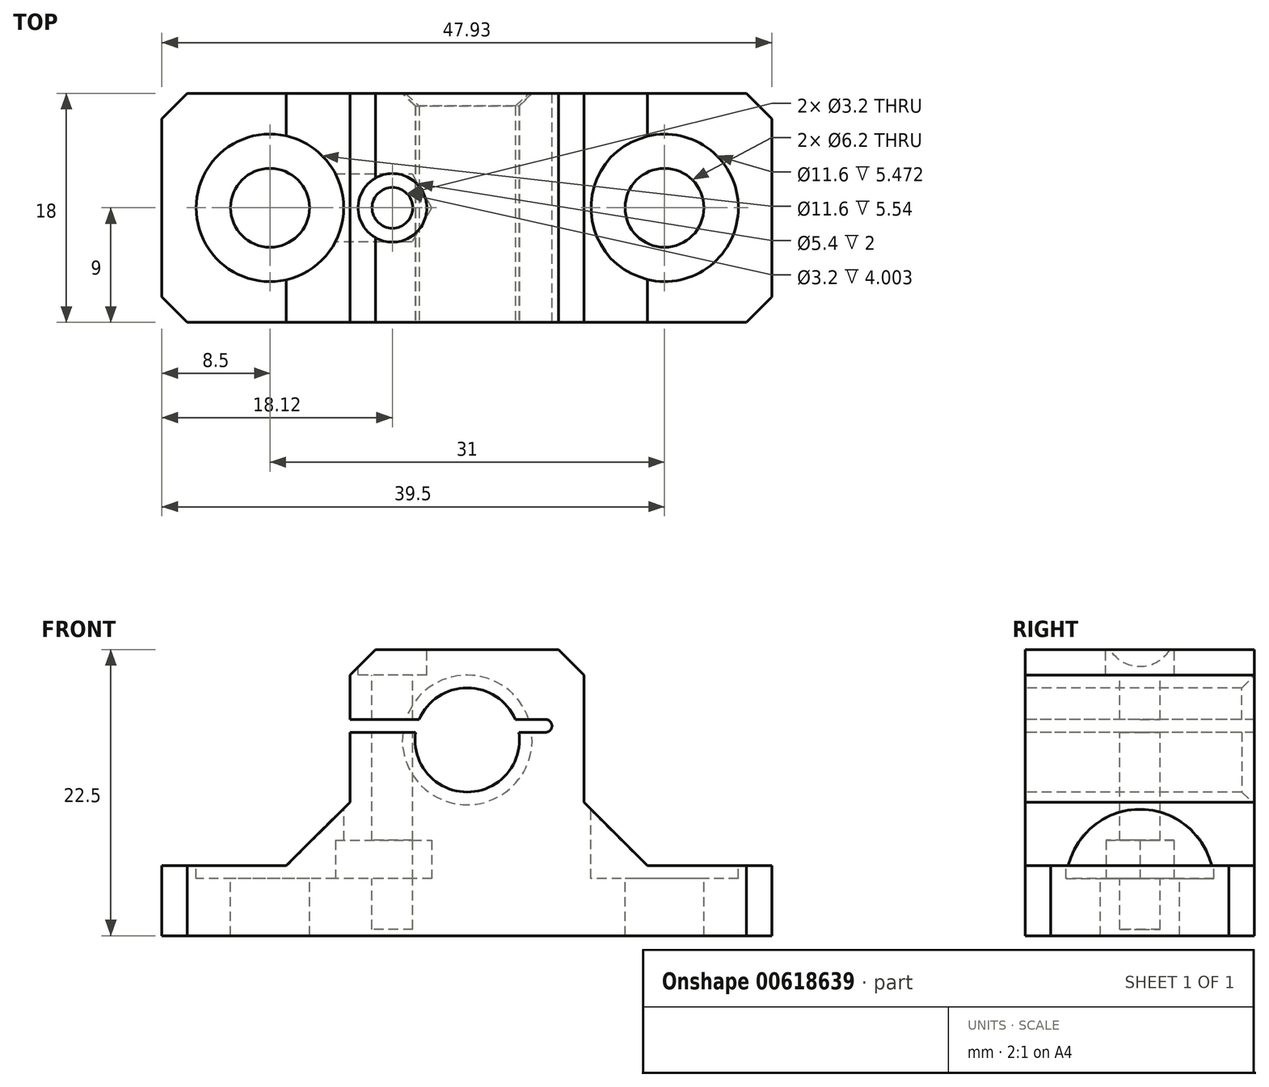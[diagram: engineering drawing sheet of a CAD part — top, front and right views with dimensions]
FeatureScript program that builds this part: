
annotation { "Feature Type Name" : "Feature", "Feature Type Description" : "" }
export const myFeature = defineFeature(function(context is Context, id is Id, definition is map)
    precondition{}
    {
        {
            var Q0;
            Q0=makeQuery(id+"FO52kGVbaD3jWPG.importOp","IMPORT",FACE,{"importTag":0.0});
            cPoint(context, id + "F0", {"pointType" : PointType.MESH_POINT, "mesh" : qUnion([Q0]), "x" : -6.2 * mm, "y" : -9.2 * mm, "z" : 8.5 * mm});
        }
        {
            var Q0;
            Q0=makeQuery(id+"FO52kGVbaD3jWPG.importOp","IMPORT",FACE,{"importTag":0.0});
            cPoint(context, id + "F1", {"pointType" : PointType.MESH_POINT, "mesh" : qUnion([Q0]), "x" : 6.2 * mm, "y" : -9.2 * mm, "z" : 8.5 * mm});
        }
        {
            var Q0;
            Q0=makeQuery(id+"FO52kGVbaD3jWPG.importOp","IMPORT",FACE,{"importTag":0.0});
            cPoint(context, id + "F2", {"pointType" : PointType.MESH_POINT, "mesh" : qUnion([Q0]), "x" : 24 * mm, "y" : -9.2 * mm, "z" : -8.5 * mm});
        }
        {
            var Q0;
            Q0=qCreatedBy(id+"F0",VERTEX);
            var Q1;
            Q1=qCreatedBy(id+"F1",VERTEX);
            var Q2;
            Q2=qCreatedBy(id+"F2",VERTEX);
            cPlane(context, id + "F3", {"entities" : qUnion([Q0, Q1, Q2]), "cplaneType" : CPlaneType.THREE_POINT, "offset" : 25 * mm, "width" : 150 * mm, "height" : 150 * mm});
        }
        {
            var Q0;
            Q0=qCreatedBy(id+"F3.planeOp",FACE);
            var sketch = newSketch(context, id + "F4", { "sketchPlane" : qUnion([Q0])});
            skPoint(sketch, "E0.0", {"position": v(-24, -8.5) * mm});
            skPoint(sketch, "E0.1", {"position": v(-24, -3) * mm});
            skPoint(sketch, "E0.2", {"position": v(-9.23, 8.5) * mm});
            skPoint(sketch, "E0.4", {"position": v(23.93, -3) * mm});
            skPoint(sketch, "E0.5", {"position": v(23.93, -8.5) * mm});
            skLineSegment(sketch, "E1", {"start": v(-24, -8.5) * mm, "end": v(-24, -3) * mm});
            skLineSegment(sketch, "E2", {"start": v(-9.23, 8.5) * mm, "end": v(-3.77, 8.5) * mm});
            skLineSegment(sketch, "E3", {"start": v(23.93, -3) * mm, "end": v(23.93, -8.5) * mm});
            skLineSegment(sketch, "E4", {"start": v(23.93, -8.5) * mm, "end": v(-24, -8.5) * mm});
            skPoint(sketch, "E5.0", {"position": v(3.77, 8.5) * mm});
            skLineSegment(sketch, "E6.bottom", {"start": v(-6.28, -8.5) * mm, "end": v(6.2, -8.5) * mm});
            skLineSegment(sketch, "E6.top", {"start": v(-6.28, -9.5) * mm, "end": v(6.2, -9.5) * mm});
            skLineSegment(sketch, "E6.left", {"start": v(-6.28, -8.5) * mm, "end": v(-6.28, -9.5) * mm});
            skLineSegment(sketch, "E6.right", {"start": v(6.2, -8.5) * mm, "end": v(6.2, -9.5) * mm});
            skLineSegment(sketch, "E7", {"start": v(9.16, 14) * mm, "end": v(9.16, -3) * mm});
            skLineSegment(sketch, "E8", {"start": v(9.16, -3) * mm, "end": v(23.93, -3) * mm});
            skLineSegment(sketch, "E9", {"start": v(-9.23, 7.5) * mm, "end": v(-9.23, -3) * mm});
            skLineSegment(sketch, "E10", {"start": v(-9.23, -3) * mm, "end": v(-24, -3) * mm});
            skPoint(sketch, "E11", {"position": v(0, 6.9) * mm});
            skArc(sketch, "E12", {"start": v(3.77, 8.5) * mm, "mid": v(0, 11) * mm, "end": v(-3.77, 8.5) * mm});
            skLineSegment(sketch, "E13.bottom", {"start": v(6.66, 8.5) * mm, "end": v(3.77, 8.5) * mm});
            skLineSegment(sketch, "E13.top", {"start": v(9.16, 14) * mm, "end": v(-9.23, 14) * mm});
            skLineSegment(sketch, "E13.right", {"start": v(-9.23, 8.5) * mm, "end": v(-9.23, 14) * mm});
            skLineSegment(sketch, "E14", {"start": v(6.66, 8.5) * mm, "end": v(6.66, 7.5) * mm});
            skLineSegment(sketch, "E15", {"start": v(6.66, 7.5) * mm, "end": v(4.05, 7.5) * mm});
            skLineSegment(sketch, "E16.trimOffspring", {"start": v(-3.77, 8.5) * mm, "end": v(-9.23, 8.5) * mm});
            skLineSegment(sketch, "E17.trimOffspring", {"start": v(-4.06, 7.5) * mm, "end": v(-9.23, 7.5) * mm});
            skLineSegment(sketch, "E18.trimOffspring", {"start": v(3.77, 8.5) * mm, "end": v(6.66, 8.5) * mm});
            skArc(sketch, "E19.trimOffspring", {"start": v(-4.06, 7.5) * mm, "mid": v(0, 2.8) * mm, "end": v(4.05, 7.5) * mm});
            skSolve(sketch);
        }
        {
            var Q0;
            Q0=makeQuery(id+"F4.imprint","IMPRINT",FACE,{"disambiguationData":[TD([[makeQuery(id+"F4.imprint","IMPRINT",EDGE,{"derivedFrom":sQuery(id+"F4.wireOp",EDGE,"E1")}),-1.0]])]});
            var Q1;
            Q1=makeQuery(id+"F4.imprint","IMPRINT",FACE,{"disambiguationData":[TD([[makeQuery(id+"F4.imprint","IMPRINT",EDGE,{"derivedFrom":sQuery(id+"F4.wireOp",EDGE,"E6.bottom")}),-1.0]])]});
            extrude(context, id + "F5", {"entities" : qUnion([Q0, Q1]), "oppositeDirection" : true, "depth" : 18 * mm, "offsetDistance" : 25 * mm});
        }
        {
            var Q0;
            Q0=makeQuery(id+"F5.opExtrude","SWEPT_FACE",FACE,{"disambiguationData":[OSD([sQuery(id+"F4.wireOp",EDGE,"E8")])]});
            var sketch = newSketch(context, id + "F6", { "sketchPlane" : qUnion([Q0])});
            skPoint(sketch, "E20.1", {"position": v(9.7, 8.8) * mm});
            skPoint(sketch, "E20.2", {"position": v(-9.7, 8.8) * mm});
            skPoint(sketch, "E20.3", {"position": v(-21.3, 8.8) * mm});
            skPoint(sketch, "E20.4", {"position": v(-21.3, -0.2) * mm});
            skPoint(sketch, "E20.5", {"position": v(-9.7, -0.2) * mm});
            skPoint(sketch, "E20.9", {"position": v(21.3, 8.8) * mm});
            skPoint(sketch, "E20.10", {"position": v(21.3, -0.2) * mm});
            skPoint(sketch, "E20.15", {"position": v(9.7, -0.2) * mm});
            skCircle(sketch, "E21", {"center": v(-15.5, -0.2) * mm, "radius": 3.1 * mm});
            skCircle(sketch, "E22", {"center": v(15.5, -0.2) * mm, "radius": 3.1 * mm});
            skCircle(sketch, "E23", {"center": v(15.5, -0.2) * mm, "radius": 5.8 * mm});
            skCircle(sketch, "E24", {"center": v(-15.5, -0.2) * mm, "radius": 5.8 * mm});
            skLineSegment(sketch, "E25", {"start": v(-21.3, -0.2) * mm, "end": v(-21.3, 8.8) * mm});
            skLineSegment(sketch, "E26", {"start": v(-21.3, 8.8) * mm, "end": v(-9.7, 8.8) * mm});
            skLineSegment(sketch, "E27", {"start": v(-9.7, 8.8) * mm, "end": v(-9.7, -0.2) * mm});
            skLineSegment(sketch, "E28", {"start": v(9.7, -0.2) * mm, "end": v(9.7, 8.8) * mm});
            skLineSegment(sketch, "E29", {"start": v(9.7, 8.8) * mm, "end": v(21.3, 8.8) * mm});
            skLineSegment(sketch, "E30", {"start": v(21.3, 8.8) * mm, "end": v(21.3, -0.2) * mm});
            skSolve(sketch);
        }
        {
            var Q0;
            Q0=makeQuery(id+"F6.imprint","IMPRINT",FACE,{"disambiguationData":[TD([[makeQuery(id+"F6.imprint","IMPRINT",EDGE,{"derivedFrom":sQuery(id+"F6.wireOp",EDGE,"E21")}),1.0]])]});
            var Q1;
            Q1=makeQuery(id+"F6.imprint","IMPRINT",FACE,{"disambiguationData":[TD([[makeQuery(id+"F6.imprint","IMPRINT",EDGE,{"derivedFrom":sQuery(id+"F6.wireOp",EDGE,"E22")}),1.0]])]});
            extrude(context, id + "F7", {"entities" : qUnion([Q0, Q1]), "operationType" : NewBodyOperationType.REMOVE, "oppositeDirection" : true, "depth" : 6 * mm, "offsetDistance" : 25 * mm});
        }
        {
            var Q0;
            Q0=makeQuery(id+"F6.imprint","IMPRINT",FACE,{"disambiguationData":[TD([[makeQuery(id+"F6.imprint","IMPRINT",EDGE,{"derivedFrom":sQuery(id+"F6.wireOp",EDGE,"E21")}),-1.0]])]});
            var Q1;
            Q1=makeQuery(id+"F6.imprint","IMPRINT",FACE,{"disambiguationData":[TD([[makeQuery(id+"F6.imprint","IMPRINT",EDGE,{"derivedFrom":sQuery(id+"F6.wireOp",EDGE,"E22")}),-1.0]])]});
            extrude(context, id + "F8", {"entities" : qUnion([Q0, Q1]), "operationType" : NewBodyOperationType.REMOVE, "oppositeDirection" : true, "depth" : 1 * mm, "offsetDistance" : 25 * mm});
        }
        {
            var Q0;
            Q0=makeQuery(id+"F5.opExtrude","SWEPT_FACE",FACE,{"disambiguationData":[OSD([sQuery(id+"F4.wireOp",EDGE,"E3")])]});
            cPlane(context, id + "F9", {"entities" : qUnion([Q0]), "cplaneType" : CPlaneType.OFFSET, "offset" : 0 * mm, "oppositeDirection" : true, "width" : 150 * mm, "height" : 150 * mm});
        }
        {
            var Q0;
            Q0=qCreatedBy(id+"F9.planeOp",FACE);
            var sketch = newSketch(context, id + "F10", { "sketchPlane" : qUnion([Q0])});
            skLineSegment(sketch, "E31", {"start": v(3.9, -10.2) * mm, "end": v(3.9, -8.89) * mm});
            skLineSegment(sketch, "E32.top", {"start": v(3.9, -8.89) * mm, "end": v(4.4, -8.89) * mm});
            skLineSegment(sketch, "E32.right", {"start": v(4.4, -8.5) * mm, "end": v(4.4, -8.89) * mm});
            skLineSegment(sketch, "E33.0", {"start": v(4.4, -8.5) * mm, "end": v(-4.8, -8.5) * mm});
            skLineSegment(sketch, "E34", {"start": v(-4.3, -10.2) * mm, "end": v(3.9, -10.2) * mm});
            skLineSegment(sketch, "E35.0", {"start": v(8.8, -8.5) * mm, "end": v(-9.2, -8.5) * mm});
            skLineSegment(sketch, "E35.1", {"start": v(-9.2, -8.5) * mm, "end": v(-9.2, -9.5) * mm});
            skLineSegment(sketch, "E35.2", {"start": v(8.8, -9.5) * mm, "end": v(-9.2, -9.5) * mm});
            skLineSegment(sketch, "E35.3", {"start": v(8.8, -8.5) * mm, "end": v(8.8, -9.5) * mm});
            skLineSegment(sketch, "E36", {"start": v(-4.8, -8.5) * mm, "end": v(-3.1, -10.2) * mm});
            skSolve(sketch);
        }
        {
            var Q0;
            {var subQ3=sQuery(id+"F10.wireOp",EDGE,"E31");Q0=makeQuery(id+"F10.imprint","IMPRINT",FACE,{"disambiguationData":[TD([[makeQuery(id+"F10.imprint","IMPRINT",EDGE,{"derivedFrom":subQ3}),-1.0]])]});}
            var Q1;
            {var subQ0=sQuery(id+"F10.wireOp",EDGE,"E35.1");Q1=makeQuery(id+"F10.imprint","IMPRINT",FACE,{"disambiguationData":[TD([[makeQuery(id+"F10.imprint","IMPRINT",EDGE,{"derivedFrom":subQ0}),1.0]])]});}
            extrude(context, id + "F11", {"entities" : qUnion([Q0, Q1]), "operationType" : NewBodyOperationType.REMOVE, "oppositeDirection" : true, "depth" : 31 * mm, "offsetDistance" : 25 * mm});
        }
        {
            var Q0;
            Q0=makeQuery(id+"F5.opExtrude","SWEPT_EDGE",EDGE,{"disambiguationData":[OSD([sQuery(id+"F4.wireOp",EDGE,"E9"),sQuery(id+"F4.wireOp",EDGE,"E10")])]});
            var Q1;
            Q1=makeQuery(id+"F5.opExtrude","SWEPT_EDGE",EDGE,{"disambiguationData":[OSD([sQuery(id+"F4.wireOp",EDGE,"E7"),sQuery(id+"F4.wireOp",EDGE,"E8")])]});
            chamfer(context, id + "F12", {"entities" : qUnion([Q0, Q1]), "width" : 5 * mm, "tangentPropagation" : true});
        }
        {
            var Q0;
            Q0=makeQuery(id+"F5.opExtrude","SWEPT_EDGE",EDGE,{"disambiguationData":[OSD([sQuery(id+"F4.wireOp",EDGE,"E13.top"),sQuery(id+"F4.wireOp",EDGE,"E13.left")])]});
            var Q1;
            Q1=makeQuery(id+"F5.opExtrude","SWEPT_EDGE",EDGE,{"disambiguationData":[OSD([sQuery(id+"F4.wireOp",EDGE,"E13.top"),sQuery(id+"F4.wireOp",EDGE,"E13.right")])]});
            var Q2;
            Q2=makeQuery(id+"F5.opExtrude","CAP_EDGE",EDGE,{"disambiguationData":[OSD([sQuery(id+"F4.wireOp",EDGE,"E1")])],"isStart":true});
            var Q3;
            Q3=makeQuery(id+"F5.opExtrude","CAP_EDGE",EDGE,{"disambiguationData":[OSD([sQuery(id+"F4.wireOp",EDGE,"E1")])],"isStart":false});
            var Q4;
            Q4=makeQuery(id+"F5.opExtrude","CAP_EDGE",EDGE,{"disambiguationData":[OSD([sQuery(id+"F4.wireOp",EDGE,"E3")])],"isStart":true});
            var Q5;
            Q5=makeQuery(id+"F5.opExtrude","CAP_EDGE",EDGE,{"disambiguationData":[OSD([sQuery(id+"F4.wireOp",EDGE,"E3")])],"isStart":false});
            chamfer(context, id + "F13", {"entities" : qUnion([Q0, Q1, Q2, Q3, Q4, Q5]), "width" : 2 * mm, "tangentPropagation" : true});
        }
        {
            var Q0;
            Q0=makeQuery(id+"F5.opExtrude","CAP_EDGE",EDGE,{"disambiguationData":[OSD([sQuery(id+"F4.wireOp",EDGE,"E19.trimOffspring")])],"isStart":false});
            var Q1;
            Q1=makeQuery(id+"F5.opExtrude","CAP_EDGE",EDGE,{"disambiguationData":[OSD([sQuery(id+"F4.wireOp",EDGE,"E12")])],"isStart":false});
            chamfer(context, id + "F14", {"entities" : qUnion([Q0, Q1]), "width" : 1 * mm, "tangentPropagation" : true});
        }
        {
            var Q0;
            Q0=makeQuery(id+"F5.opExtrude","SWEPT_EDGE",EDGE,{"disambiguationData":[OSD([sQuery(id+"F4.wireOp",EDGE,"E14"),sQuery(id+"F4.wireOp",EDGE,"E15")])]});
            var Q1;
            Q1=makeQuery(id+"F5.opExtrude","SWEPT_EDGE",EDGE,{"disambiguationData":[OSD([sQuery(id+"F4.wireOp",EDGE,"E14"),sQuery(id+"F4.wireOp",EDGE,"E18.trimOffspring")])]});
            fillet(context, id + "F15", {"entities" : qUnion([Q0, Q1]), "radius" : 0.5 * mm, "tangentPropagation" : true, "allowEdgeOverflow" : false});
        }
        {
            var Q0;
            Q0=makeQuery(id+"F5.opExtrude","SWEPT_FACE",FACE,{"disambiguationData":[OSD([sQuery(id+"F4.wireOp",EDGE,"E13.top")])]});
            var sketch = newSketch(context, id + "F16", { "sketchPlane" : qUnion([Q0])});
            skLineSegment(sketch, "E37.0", {"start": v(-7.23, 7.8) * mm, "end": v(-7.23, -8.2) * mm, "construction": true});
            skLineSegment(sketch, "E38", {"start": v(-7.23, -0.2) * mm, "end": v(-5.88, -0.2) * mm, "construction": true});
            skCircle(sketch, "E39", {"center": v(-5.88, -0.2) * mm, "radius": 1.6 * mm});
            skCircle(sketch, "E40", {"center": v(-5.88, -0.2) * mm, "radius": 2.7 * mm});
            skSolve(sketch);
        }
        {
            var Q0;
            Q0=makeQuery(id+"F16.imprint","IMPRINT",FACE,{"disambiguationData":[TD([[makeQuery(id+"F16.imprint","IMPRINT",EDGE,{"derivedFrom":sQuery(id+"F16.wireOp",EDGE,"E39")}),1.0]])]});
            extrude(context, id + "F17", {"entities" : qUnion([Q0]), "operationType" : NewBodyOperationType.REMOVE, "oppositeDirection" : true, "depth" : 22 * mm, "offsetDistance" : 25 * mm});
        }
        {
            var Q0;
            {var subQ0=sQuery(id+"F16.wireOp",EDGE,"E40");var subQ1=sQuery(id+"F4.wireOp",EDGE,"E13.top");var subQ2=makeQuery(id+"F13.opChamfer","BLEND_EDGE",EDGE,{"blendedFrom":[makeQuery(id+"F5.opExtrude","SWEPT_EDGE",EDGE,{"disambiguationData":[OSD([subQ1,sQuery(id+"F4.wireOp",EDGE,"E13.right")])]}),makeQuery(id+"F5.opExtrude","SWEPT_FACE",FACE,{"disambiguationData":[OSD([subQ1])]})],"blendedInto":[makeQuery(id+"F5.opExtrude","SWEPT_FACE",FACE,{"disambiguationData":[OSD([subQ1])]})]});var subQ3=makeQuery(id+"F16.imprint","INTERSECT",VERTEX,{"disambiguationData":[OD(0.0)],"derivedFrom":[subQ2,subQ0]});Q0=makeQuery(id+"F16.imprint","IMPRINT",FACE,{"disambiguationData":[TD([[makeQuery(id+"F16.imprint","IMPRINT",EDGE,{"disambiguationData":[TD([[subQ3,1.0]])],"derivedFrom":subQ0}),1.0]])]});}
            var Q1;
            Q1=makeQuery(id+"F16.imprint","IMPRINT",FACE,{"disambiguationData":[TD([[makeQuery(id+"F16.imprint","IMPRINT",EDGE,{"derivedFrom":sQuery(id+"F16.wireOp",EDGE,"E39")}),-1.0]])]});
            extrude(context, id + "F18", {"entities" : qUnion([Q0, Q1]), "operationType" : NewBodyOperationType.REMOVE, "oppositeDirection" : true, "depth" : 2 * mm, "offsetDistance" : 25 * mm});
        }
        {
            var Q0;
            Q0=makeQuery(id+"F8.boolean.opBoolean","COPY",FACE,{"derivedFrom":makeQuery(id+"F8.opExtrude","CAP_FACE",FACE,{"disambiguationData":[OSD([sQuery(id+"F6.wireOp",EDGE,"E21"),sQuery(id+"F6.wireOp",EDGE,"E24")])],"isStart":false})});
            var sketch = newSketch(context, id + "F19", { "sketchPlane" : qUnion([Q0])});
            skPoint(sketch, "E41.0", {"position": v(-5.88, -0.2) * mm});
            skCircle(sketch, "E42.cCircle", {"center": v(-5.88, -0.2) * mm, "radius": 2.67 * mm, "construction": true});
            skLineSegment(sketch, "E42.0", {"start": v(-4.34, -2.88) * mm, "end": v(-7.42, -2.88) * mm});
            skLineSegment(sketch, "E42.1", {"start": v(-7.42, -2.88) * mm, "end": v(-8.97, -0.2) * mm});
            skLineSegment(sketch, "E42.2", {"start": v(-8.97, -0.2) * mm, "end": v(-7.42, 2.47) * mm});
            skLineSegment(sketch, "E42.3", {"start": v(-7.42, 2.47) * mm, "end": v(-4.34, 2.47) * mm});
            skLineSegment(sketch, "E42.4", {"start": v(-4.34, 2.47) * mm, "end": v(-2.8, -0.2) * mm});
            skLineSegment(sketch, "E42.5", {"start": v(-2.8, -0.2) * mm, "end": v(-4.34, -2.88) * mm});
            skPoint(sketch, "E42.0.midPoint", {"position": v(-5.88, -2.88) * mm});
            skCircle(sketch, "E43", {"center": v(-5.88, -0.2) * mm, "radius": 1.5 * mm});
            skLineSegment(sketch, "E44", {"start": v(-7.42, 2.47) * mm, "end": v(-14.13, 2.47) * mm});
            skLineSegment(sketch, "E45", {"start": v(-14.13, 2.47) * mm, "end": v(-14.13, -2.88) * mm});
            skLineSegment(sketch, "E46", {"start": v(-14.13, -2.88) * mm, "end": v(-7.42, -2.88) * mm});
            skSolve(sketch);
        }
        {
            var Q0;
            Q0=makeQuery(id+"F19.imprint","IMPRINT",FACE,{"disambiguationData":[TD([[makeQuery(id+"F19.imprint","IMPRINT",EDGE,{"derivedFrom":sQuery(id+"F19.wireOp",EDGE,"E42.0")}),-1.0]])]});
            var Q1;
            Q1=makeQuery(id+"F19.imprint","IMPRINT",FACE,{"disambiguationData":[TD([[makeQuery(id+"F19.imprint","IMPRINT",EDGE,{"derivedFrom":sQuery(id+"F19.wireOp",EDGE,"E42.1")}),1.0]])]});
            extrude(context, id + "F20", {"entities" : qUnion([Q0, Q1]), "operationType" : NewBodyOperationType.REMOVE, "depth" : 3 * mm, "offsetDistance" : 25 * mm});
        }
    });
